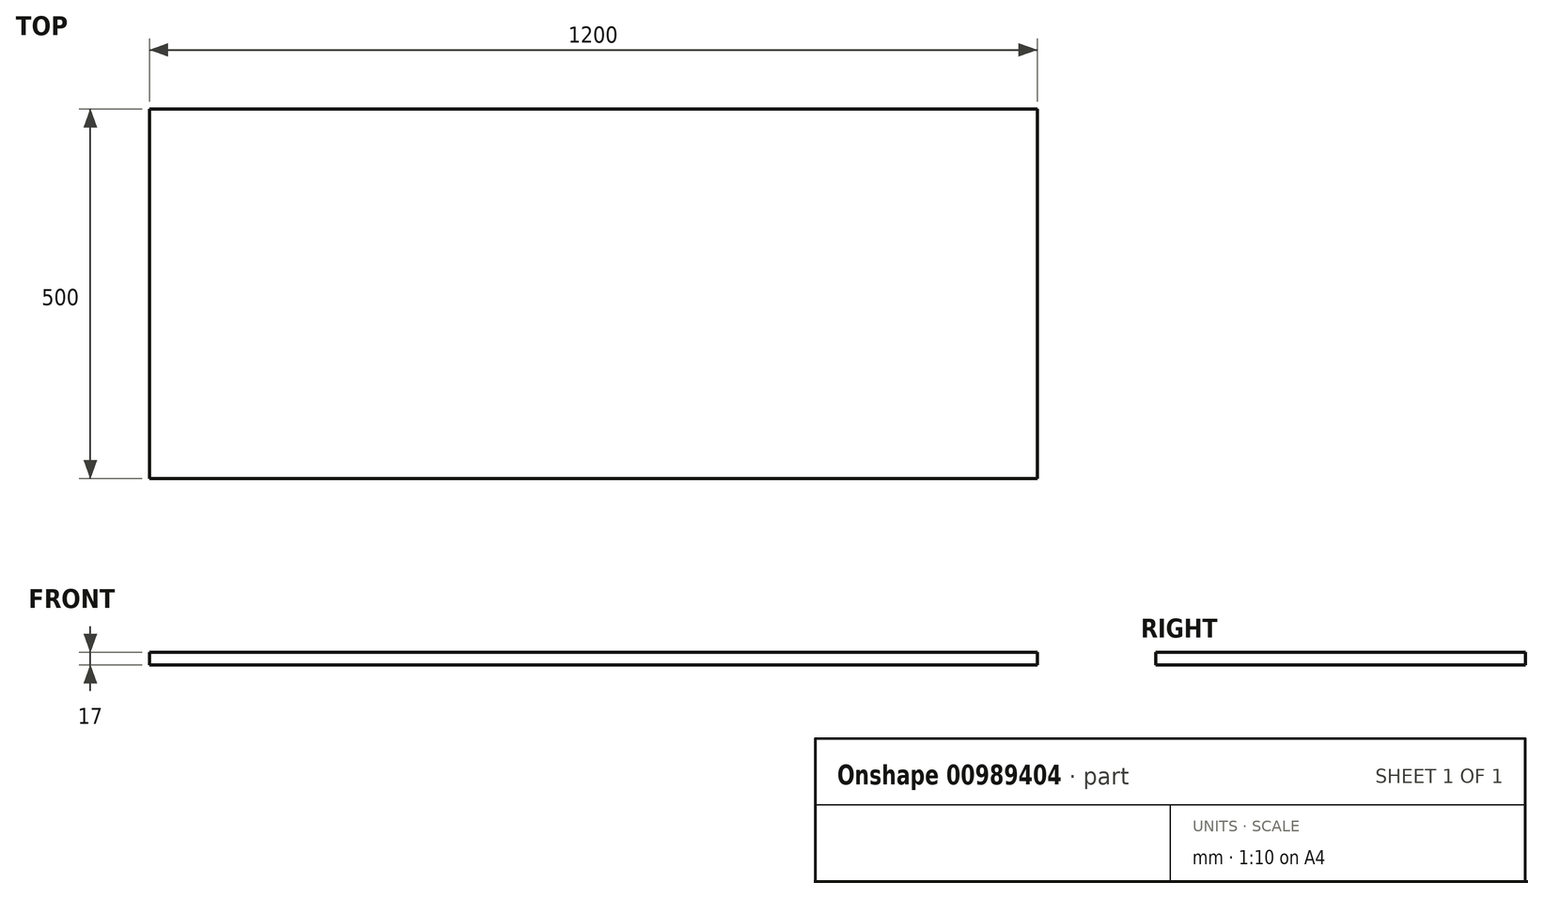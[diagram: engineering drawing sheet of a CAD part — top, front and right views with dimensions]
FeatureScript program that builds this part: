
annotation { "Feature Type Name" : "Feature", "Feature Type Description" : "" }
export const myFeature = defineFeature(function(context is Context, id is Id, definition is map)
    precondition{}
    {
        {
            var Q0;
            Q0=qCreatedBy(makeId("Top.planeOp"),FACE);
            var sketch = newSketch(context, id + "F0", { "sketchPlane" : qUnion([Q0])});
            skLineSegment(sketch, "E0.bottom", {"start": v(540.38, -18.63) * mm, "end": v(-659.62, -18.63) * mm});
            skLineSegment(sketch, "E0.top", {"start": v(540.38, 481.37) * mm, "end": v(-659.62, 481.37) * mm});
            skLineSegment(sketch, "E0.left", {"start": v(540.38, -18.63) * mm, "end": v(540.38, 481.37) * mm});
            skLineSegment(sketch, "E0.right", {"start": v(-659.62, -18.63) * mm, "end": v(-659.62, 481.37) * mm});
            skPoint(sketch, "E0.middle", {"position": v(-59.62, 231.37) * mm});
            skSolve(sketch);
        }
        {
            var Q0;
            Q0 = qSketchRegion(id + "F0", true);
            var Q1;
            Q1=makeQuery(id+"F0.imprint","IMPRINT",FACE,{"disambiguationData":[TD([[makeQuery(id+"F0.imprint","IMPRINT",EDGE,{"derivedFrom":sQuery(id+"F0.wireOp",EDGE,"E0.bottom")}),-1.0]])]});
            extrude(context, id + "F1", {"entities" : qUnion([Q0, Q1]), "depth" : 17 * mm, "offsetDistance" : 25 * mm});
        }
    });
